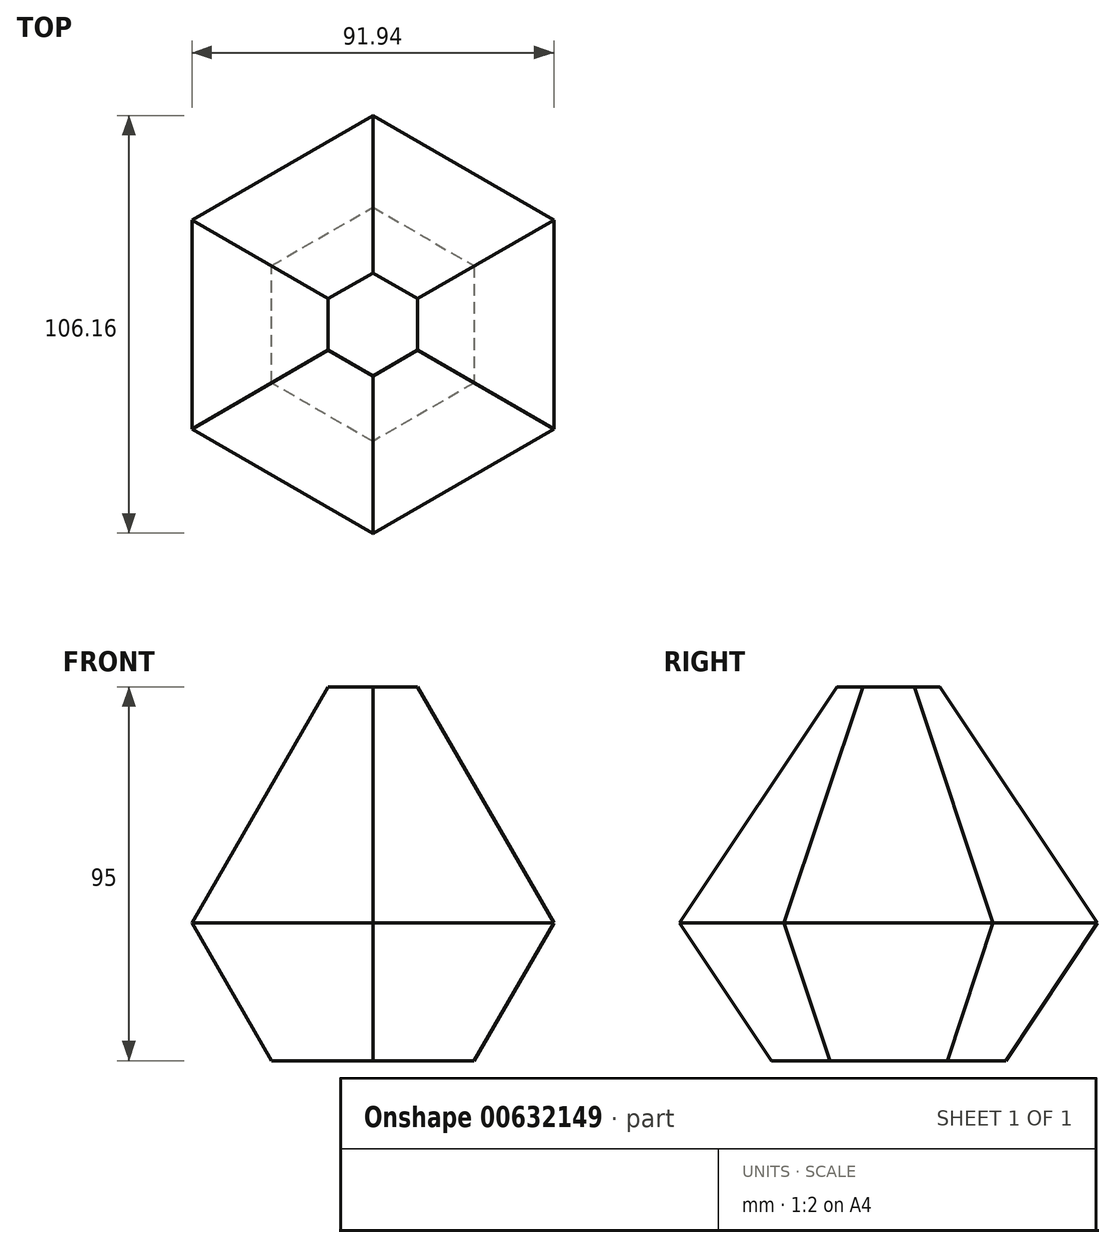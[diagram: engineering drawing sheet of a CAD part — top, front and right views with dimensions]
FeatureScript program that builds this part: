
annotation { "Feature Type Name" : "Feature", "Feature Type Description" : "" }
export const myFeature = defineFeature(function(context is Context, id is Id, definition is map)
    precondition{}
    {
        {
            var Q0;
            Q0=qCreatedBy(makeId("Top.planeOp"),FACE);
            var sketch = newSketch(context, id + "F0", { "sketchPlane" : qUnion([Q0])});
            skCircle(sketch, "E0.cCircle", {"center": v(0, 0) * mm, "radius": 29.75 * mm, "construction": true});
            skLineSegment(sketch, "E0.0", {"start": v(0, -29.75) * mm, "end": v(-25.76, -14.87) * mm});
            skLineSegment(sketch, "E0.1", {"start": v(-25.76, -14.88) * mm, "end": v(-25.76, 14.87) * mm});
            skLineSegment(sketch, "E0.2", {"start": v(-25.76, 14.87) * mm, "end": v(0, 29.75) * mm});
            skLineSegment(sketch, "E0.3", {"start": v(0, 29.75) * mm, "end": v(25.76, 14.88) * mm});
            skLineSegment(sketch, "E0.4", {"start": v(25.76, 14.88) * mm, "end": v(25.76, -14.87) * mm});
            skLineSegment(sketch, "E0.5", {"start": v(25.76, -14.87) * mm, "end": v(0, -29.75) * mm});
            skSolve(sketch);
        }
        {
            var Q0;
            Q0=makeQuery(id+"F0.imprint","IMPRINT",FACE,{"disambiguationData":[TD([[makeQuery(id+"F0.imprint","IMPRINT",EDGE,{"derivedFrom":sQuery(id+"F0.wireOp",EDGE,"E0.0")}),-1.0]])]});
            extrude(context, id + "F1", {"entities" : qUnion([Q0]), "depth" : 35 * mm, "offsetDistance" : 25 * mm, "hasDraft" : true, "draftAngle" : 30 * degree});
        }
        {
            var Q0;
            Q0=makeQuery(id+"F1.opExtrude","CAP_FACE",FACE,{"disambiguationData":[OSD([sQuery(id+"F0.wireOp",EDGE,"E0.0"),sQuery(id+"F0.wireOp",EDGE,"E0.1"),sQuery(id+"F0.wireOp",EDGE,"E0.2"),sQuery(id+"F0.wireOp",EDGE,"E0.3"),sQuery(id+"F0.wireOp",EDGE,"E0.4"),sQuery(id+"F0.wireOp",EDGE,"E0.5")])],"isStart":false});
            extrude(context, id + "F2", {"entities" : qUnion([Q0]), "operationType" : NewBodyOperationType.ADD, "depth" : 60 * mm, "offsetDistance" : 25 * mm, "hasDraft" : true, "draftAngle" : 30 * degree, "draftPullDirection" : true});
        }
    });
